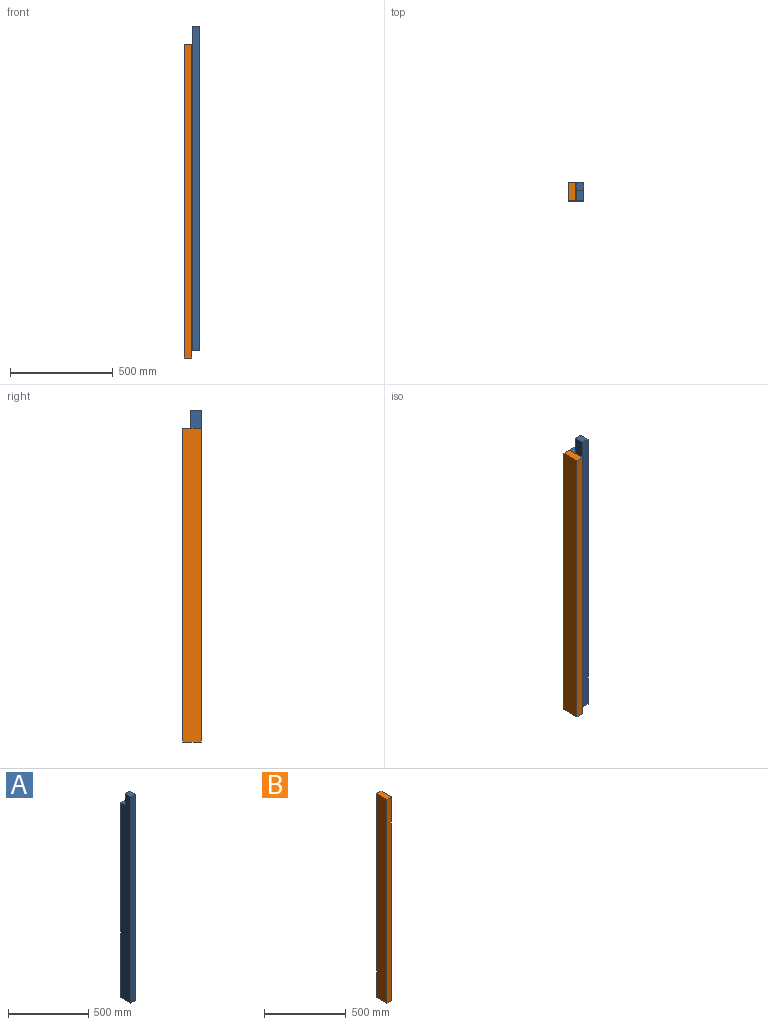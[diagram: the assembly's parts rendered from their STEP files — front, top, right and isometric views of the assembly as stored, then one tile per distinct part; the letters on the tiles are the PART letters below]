
ASSEMBLY  parts=2 mates=1
PART A: 8 faces, bbox 38.1x88.9x1574.8 mm
  f0: plane 1485.9x38.1mm, normal (0,1,0), area 56612.8mm2, adj f1,f5,f6,f7
  f1: plane 88.9x38.1mm, normal (0,0,-1), area 3387.1mm2, adj f0,f2,f6,f7
  f2: plane 1574.8x38.1mm, normal (0,-1,0), area 59999.9mm2, adj f1,f3,f6,f7
  f3: plane 50.8x38.1mm, normal (0,0,1), area 1935.5mm2, adj f2,f4,f6,f7
  f4: plane 88.9x38.1mm, normal (0,1,0), area 3387.1mm2, adj f3,f5,f6,f7
  f5: plane 38.1x38.1mm, normal (0,0,1), area 1451.6mm2, adj f0,f4,f6,f7
  f6: plane 1574.8x88.9mm, normal (-1,0,0), area 136612.6mm2, adj f0,f1,f2,f3,f4,f5
  f7: plane 1574.8x88.9mm, normal (1,0,0), area 136612.6mm2, adj f0,f1,f2,f3,f4,f5
PART B: 6 faces, bbox 38.1x88.9x1524 mm
  f0: plane 1524x38.1mm, normal (0,-1,0), area 58064.4mm2, adj f1,f3,f4,f5
  f1: plane 88.9x38.1mm, normal (0,0,-1), area 3387.1mm2, adj f0,f2,f4,f5
  f2: plane 1524x38.1mm, normal (0,1,0), area 58064.4mm2, adj f1,f3,f4,f5
  f3: plane 88.9x38.1mm, normal (0,0,1), area 3387.1mm2, adj f0,f2,f4,f5
  f4: plane 1524x88.9mm, normal (-1,0,0), area 135483.6mm2, adj f0,f1,f2,f3
  f5: plane 1524x88.9mm, normal (1,0,0), area 135483.6mm2, adj f0,f1,f2,f3
PLACE A t=(7.43,-958.98,-715.01)mm
PLACE B t=(858.33,831.72,-715.01)mm
MATE fastened A.f5 <-> B.f3  axis (0,0,1) through (-564.07,653.92,834.39)mm
